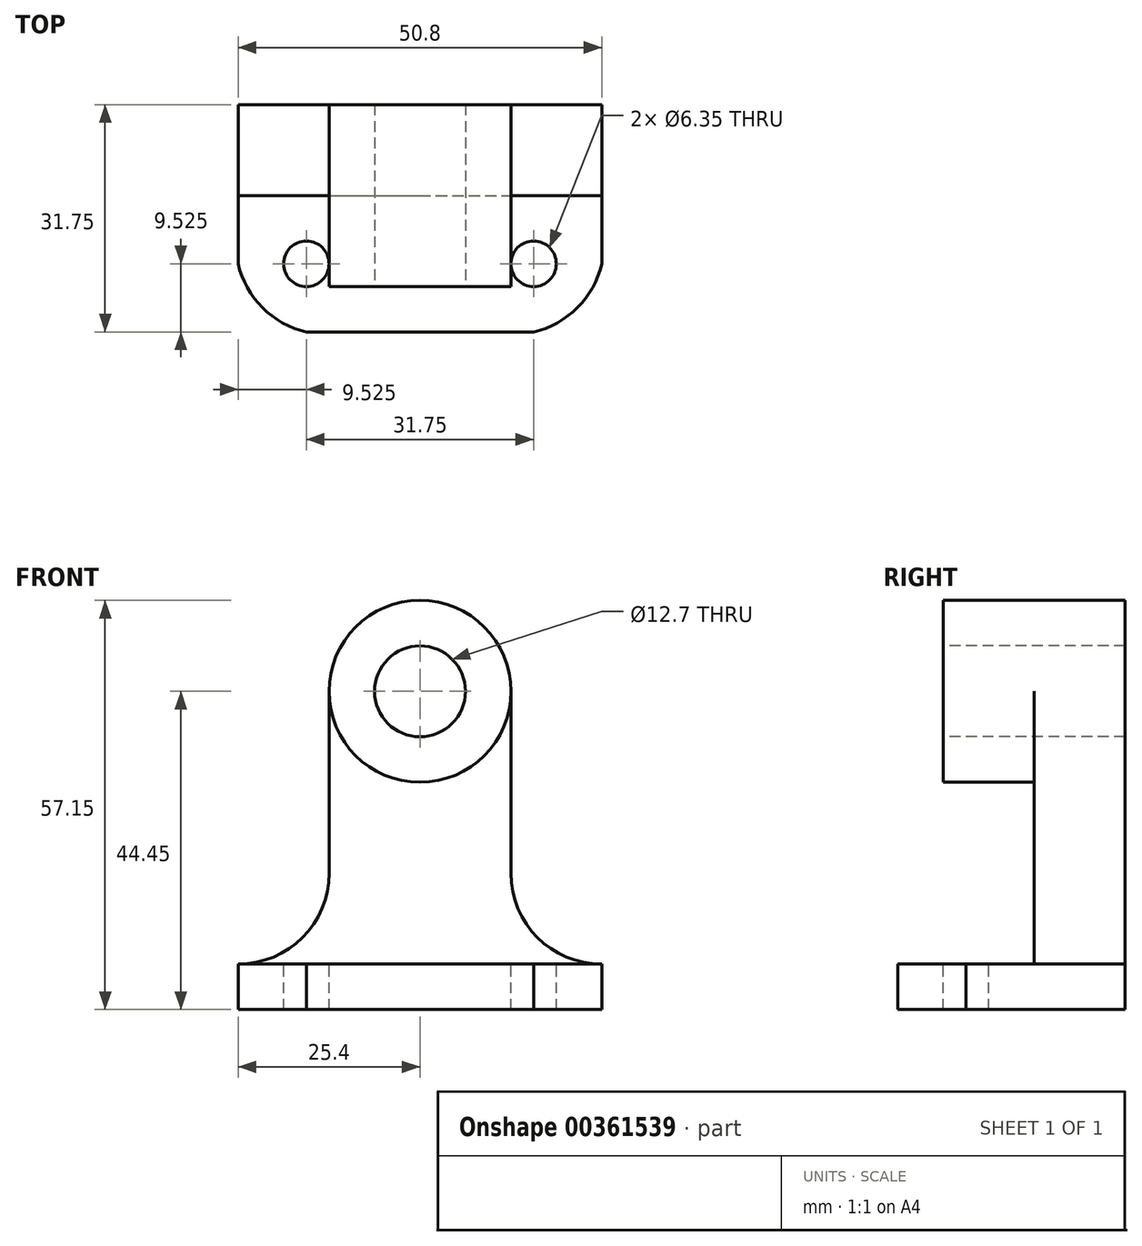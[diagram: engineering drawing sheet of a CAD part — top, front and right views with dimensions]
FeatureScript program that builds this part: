
annotation { "Feature Type Name" : "Feature", "Feature Type Description" : "" }
export const myFeature = defineFeature(function(context is Context, id is Id, definition is map)
    precondition{}
    {
        {
            var Q0;
            Q0=qCreatedBy(makeId("Top.planeOp"),FACE);
            var sketch = newSketch(context, id + "F0", { "sketchPlane" : qUnion([Q0])});
            skLineSegment(sketch, "E0.bottom", {"start": v(0, 31.75) * mm, "end": v(50.8, 31.75) * mm});
            skLineSegment(sketch, "E0.top", {"start": v(0, 0) * mm, "end": v(50.8, 0) * mm});
            skLineSegment(sketch, "E0.left", {"start": v(0, 31.75) * mm, "end": v(0, 0) * mm});
            skLineSegment(sketch, "E0.right", {"start": v(50.8, 31.75) * mm, "end": v(50.8, 0) * mm});
            skSolve(sketch);
        }
        {
            var Q0;
            Q0 = qSketchRegion(id + "F0", true);
            extrude(context, id + "F1", {"entities" : qUnion([Q0]), "depth" : 6.35 * mm});
        }
        {
            var Q0;
            Q0=makeQuery(id+"F1.opExtrude","CAP_FACE",FACE,{"disambiguationData":[OSD([sQuery(id+"F0.wireOp",EDGE,"E0.bottom"),sQuery(id+"F0.wireOp",EDGE,"E0.top"),sQuery(id+"F0.wireOp",EDGE,"E0.left"),sQuery(id+"F0.wireOp",EDGE,"E0.right")])],"isStart":false});
            var sketch = newSketch(context, id + "F2", { "sketchPlane" : qUnion([Q0])});
            skCircle(sketch, "E1", {"center": v(9.53, 9.53) * mm, "radius": 3.18 * mm});
            skCircle(sketch, "E2", {"center": v(41.28, 9.53) * mm, "radius": 3.18 * mm});
            skArc(sketch, "E3", {"start": v(0, 9.52) * mm, "mid": v(3.4, 3.4) * mm, "end": v(9.52, 0) * mm});
            skArc(sketch, "E4", {"start": v(41.28, 0) * mm, "mid": v(47.4, 3.4) * mm, "end": v(50.8, 9.53) * mm});
            skSolve(sketch);
        }
        {
            var Q0;
            Q0=makeQuery(id+"F2.imprint","IMPRINT",FACE,{"disambiguationData":[TD([[makeQuery(id+"F2.imprint","IMPRINT",EDGE,{"derivedFrom":sQuery(id+"F2.wireOp",EDGE,"E2")}),1.0]])]});
            var Q1;
            Q1=makeQuery(id+"F2.imprint","IMPRINT",FACE,{"disambiguationData":[TD([[makeQuery(id+"F2.imprint","IMPRINT",EDGE,{"derivedFrom":sQuery(id+"F2.wireOp",EDGE,"E1")}),1.0]])]});
            var Q2;
            {var subQ0=sQuery(id+"F2.wireOp",EDGE,"E3");Q2=makeQuery(id+"F2.imprint","IMPRINT",FACE,{"disambiguationData":[TD([[makeQuery(id+"F2.imprint","IMPRINT",EDGE,{"derivedFrom":subQ0}),-1.0]])]});}
            var Q3;
            {var subQ0=sQuery(id+"F2.wireOp",EDGE,"E4");Q3=makeQuery(id+"F2.imprint","IMPRINT",FACE,{"disambiguationData":[TD([[makeQuery(id+"F2.imprint","IMPRINT",EDGE,{"derivedFrom":subQ0}),-1.0]])]});}
            extrude(context, id + "F3", {"entities" : qUnion([Q0, Q1, Q2, Q3]), "operationType" : NewBodyOperationType.REMOVE, "oppositeDirection" : true, "depth" : 6.35 * mm});
        }
        {
            var Q0;
            Q0=makeQuery(id+"F1.opExtrude","CAP_FACE",FACE,{"disambiguationData":[OSD([sQuery(id+"F0.wireOp",EDGE,"E0.bottom"),sQuery(id+"F0.wireOp",EDGE,"E0.top"),sQuery(id+"F0.wireOp",EDGE,"E0.left"),sQuery(id+"F0.wireOp",EDGE,"E0.right")])],"isStart":false});
            var sketch = newSketch(context, id + "F4", { "sketchPlane" : qUnion([Q0])});
            skLineSegment(sketch, "E5.bottom", {"start": v(0, 31.75) * mm, "end": v(50.8, 31.75) * mm});
            skLineSegment(sketch, "E5.top", {"start": v(0, 19.05) * mm, "end": v(50.8, 19.05) * mm});
            skLineSegment(sketch, "E5.left", {"start": v(0, 31.75) * mm, "end": v(0, 19.05) * mm});
            skLineSegment(sketch, "E5.right", {"start": v(50.8, 31.75) * mm, "end": v(50.8, 19.05) * mm});
            skSolve(sketch);
        }
        {
            var Q0;
            Q0 = qSketchRegion(id + "F4", true);
            extrude(context, id + "F5", {"entities" : qUnion([Q0]), "operationType" : NewBodyOperationType.ADD, "depth" : 57.15 * mm});
        }
        {
            var Q0;
            Q0=makeQuery(id+"F5.opExtrude","SWEPT_FACE",FACE,{"disambiguationData":[OSD([sQuery(id+"F4.wireOp",EDGE,"E5.top")])]});
            var sketch = newSketch(context, id + "F6", { "sketchPlane" : qUnion([Q0])});
            skCircle(sketch, "E6", {"center": v(25.4, 44.45) * mm, "radius": 12.7 * mm});
            skLineSegment(sketch, "E7", {"start": v(38.1, 44.45) * mm, "end": v(38.1, 19.05) * mm});
            skArc(sketch, "E8", {"start": v(38.1, 19.05) * mm, "mid": v(41.82, 10.07) * mm, "end": v(50.8, 6.35) * mm});
            skLineSegment(sketch, "E9", {"start": v(12.7, 44.45) * mm, "end": v(12.7, 19.05) * mm});
            skArc(sketch, "E10", {"start": v(0, 6.35) * mm, "mid": v(8.98, 10.07) * mm, "end": v(12.7, 19.05) * mm});
            skLineSegment(sketch, "E11", {"start": v(0, 6.35) * mm, "end": v(0, 63.5) * mm});
            skLineSegment(sketch, "E12", {"start": v(0, 63.5) * mm, "end": v(50.8, 63.5) * mm});
            skLineSegment(sketch, "E13", {"start": v(51.6, 62.99) * mm, "end": v(50.8, 6.35) * mm});
            skSolve(sketch);
        }
        {
            var Q0;
            {var subQ1=sQuery(id+"F6.wireOp",EDGE,"E7");Q0=makeQuery(id+"F6.imprint","IMPRINT",FACE,{"disambiguationData":[TD([[makeQuery(id+"F6.imprint","IMPRINT",EDGE,{"derivedFrom":subQ1}),1.0]])]});}
            extrude(context, id + "F7", {"entities" : qUnion([Q0]), "operationType" : NewBodyOperationType.REMOVE, "oppositeDirection" : true, "depth" : 12.7 * mm});
        }
        {
            var Q0;
            {var subQ0=sQuery(id+"F6.wireOp",EDGE,"E6");var subQ1=makeQuery(id+"F6.imprint","INTERSECT",VERTEX,{"derivedFrom":[subQ0,sQuery(id+"F6.wireOp",EDGE,"E7")]});Q0=makeQuery(id+"F6.imprint","IMPRINT",FACE,{"disambiguationData":[TD([[makeQuery(id+"F6.imprint","IMPRINT",EDGE,{"disambiguationData":[TD([[subQ1,-1.0]])],"derivedFrom":subQ0}),1.0]])]});}
            extrude(context, id + "F8", {"entities" : qUnion([Q0]), "operationType" : NewBodyOperationType.ADD, "depth" : 12.7 * mm});
        }
        {
            var Q0;
            Q0=makeQuery(id+"F8.opExtrude","CAP_FACE",FACE,{"disambiguationData":[OSD([sQuery(id+"F6.wireOp",EDGE,"E6")])],"isStart":false});
            var sketch = newSketch(context, id + "F9", { "sketchPlane" : qUnion([Q0])});
            skCircle(sketch, "E14", {"center": v(25.4, 44.45) * mm, "radius": 6.35 * mm});
            skSolve(sketch);
        }
        {
            var Q0;
            Q0 = qSketchRegion(id + "F9", true);
            extrude(context, id + "F10", {"entities" : qUnion([Q0]), "operationType" : NewBodyOperationType.REMOVE, "oppositeDirection" : true, "depth" : 38.1 * mm});
        }
    });
